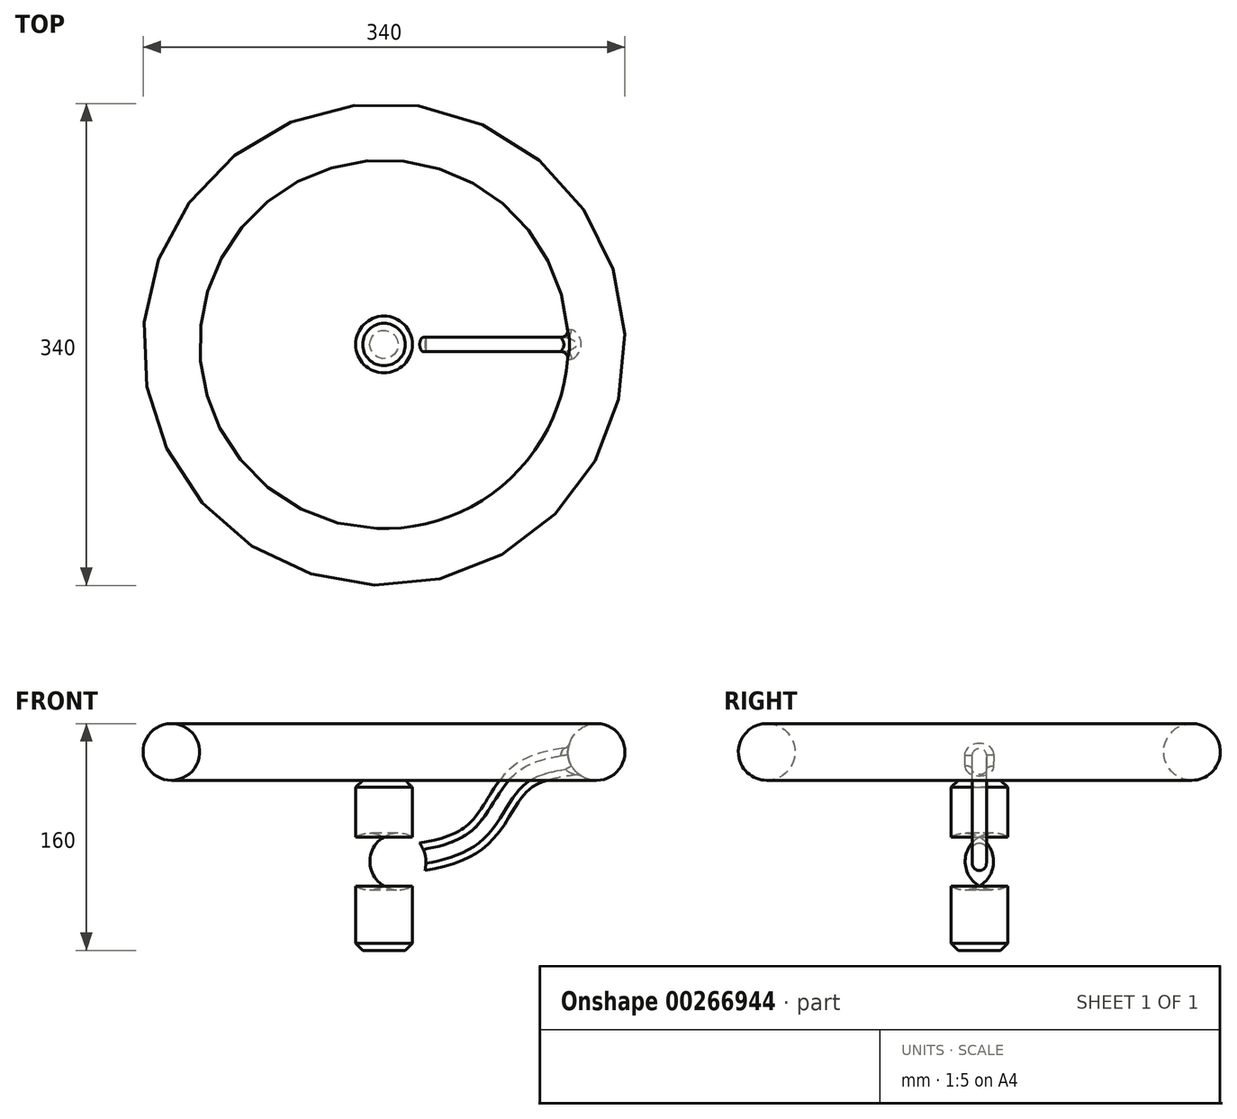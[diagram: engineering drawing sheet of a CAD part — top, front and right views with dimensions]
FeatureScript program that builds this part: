
annotation { "Feature Type Name" : "Feature", "Feature Type Description" : "" }
export const myFeature = defineFeature(function(context is Context, id is Id, definition is map)
    precondition{}
    {
        {
            var Q0;
            Q0=qCreatedBy(makeId("Front.planeOp"),FACE);
            var sketch = newSketch(context, id + "F0", { "sketchPlane" : qUnion([Q0])});
            skLineSegment(sketch, "E0", {"start": v(0, 60) * mm, "end": v(0, -60) * mm});
            skLineSegment(sketch, "E1", {"start": v(0, -60) * mm, "end": v(20, -60) * mm});
            skLineSegment(sketch, "E2", {"start": v(20, -60) * mm, "end": v(20, -14.64) * mm});
            skLineSegment(sketch, "E3", {"start": v(0, 60) * mm, "end": v(20, 60) * mm});
            skLineSegment(sketch, "E4", {"start": v(20, 60) * mm, "end": v(20, 20) * mm});
            skArc(sketch, "E5", {"start": v(20, -14.64) * mm, "mid": v(30, 2.68) * mm, "end": v(20, 20) * mm});
            skSolve(sketch);
        }
        {
            var Q0;
            Q0 = qSketchRegion(id + "F0", true);
            var Q1;
            Q1=sQuery(id+"F0.wireOp",EDGE,"E0");
            revolve(context, id + "F1", {"entities" : qUnion([Q0]), "axis" : qUnion([Q1]), "revolveType" : RevolveType.FULL});
        }
        {
            var Q0;
            Q0=makeQuery(id+"F1.opRevolve","SWEPT_EDGE",EDGE,{"disambiguationData":[OSD([sQuery(id+"F0.wireOp",EDGE,"E3"),sQuery(id+"F0.wireOp",EDGE,"E4")])]});
            var Q1;
            Q1=makeQuery(id+"F1.opRevolve","SWEPT_EDGE",EDGE,{"disambiguationData":[OSD([sQuery(id+"F0.wireOp",EDGE,"E1"),sQuery(id+"F0.wireOp",EDGE,"E2")])]});
            chamfer(context, id + "F2", {"entities" : qUnion([Q0, Q1]), "width" : 5 * mm, "tangentPropagation" : true});
        }
        {
            var Q0;
            Q0=qCreatedBy(makeId("Right.planeOp"),FACE);
            cPlane(context, id + "F3", {"entities" : qUnion([Q0]), "cplaneType" : CPlaneType.OFFSET, "offset" : 20 * mm, "width" : 150 * mm, "height" : 150 * mm});
        }
        {
            var Q0;
            Q0=qCreatedBy(id+"F3.planeOp",FACE);
            var sketch = newSketch(context, id + "F4", { "sketchPlane" : qUnion([Q0])});
            skLineSegment(sketch, "E6.bottom", {"start": v(0, -5) * mm, "end": v(0, -5) * mm});
            skLineSegment(sketch, "E6.top", {"start": v(0, 15) * mm, "end": v(0, 15) * mm});
            skLineSegment(sketch, "E6.left", {"start": v(5, 0) * mm, "end": v(5, 10) * mm});
            skLineSegment(sketch, "E6.right", {"start": v(-5, 0) * mm, "end": v(-5, 10) * mm});
            skPoint(sketch, "E6.middle", {"position": v(0, 5) * mm});
            skPoint(sketch, "E7.visualSharp", {"position": v(5, 15) * mm});
            skArc(sketch, "E7.filletArc", {"start": v(5, 10) * mm, "mid": v(3.54, 13.54) * mm, "end": v(0, 15) * mm});
            skPoint(sketch, "E8.visualSharp", {"position": v(-5, 15) * mm});
            skArc(sketch, "E8.filletArc", {"start": v(0, 15) * mm, "mid": v(-3.54, 13.54) * mm, "end": v(-5, 10) * mm});
            skPoint(sketch, "E9.visualSharp", {"position": v(-5, -5) * mm});
            skArc(sketch, "E9.filletArc", {"start": v(-5, 0) * mm, "mid": v(-3.54, -3.54) * mm, "end": v(0, -5) * mm});
            skPoint(sketch, "E10.visualSharp", {"position": v(5, -5) * mm});
            skArc(sketch, "E10.filletArc", {"start": v(0, -5) * mm, "mid": v(3.54, -3.54) * mm, "end": v(5, 0) * mm});
            skSolve(sketch);
        }
        {
            var Q0;
            Q0=qCreatedBy(makeId("Front.planeOp"),FACE);
            var sketch = newSketch(context, id + "F5", { "sketchPlane" : qUnion([Q0])});
            skFitSpline(sketch, "E11", {"points": [v(20.08, 5.28) * mm, v(66.4, 22.18) * mm, v(96.37, 61.72) * mm, v(150, 76.2) * mm], "startDerivative": vector(146.82, 19.14) * mm, "endDerivative": vector(191.33, 30.59) * mm});
            skSolve(sketch);
        }
        {
            var Q0;
            Q0 = qSketchRegion(id + "F4", true);
            var Q1;
            Q1 = qConstructionFilter(qBodyType(qCreatedBy(id + "F5" ,EDGE), BodyType.WIRE), ConstructionObject.NO);
            sweep(context, id + "F6", {"operationType" : NewBodyOperationType.ADD, "profiles" : qUnion([Q0]), "path" : qUnion([Q1])});
        }
        {
            var Q0;
            Q0=qCreatedBy(makeId("Front.planeOp"),FACE);
            var sketch = newSketch(context, id + "F7", { "sketchPlane" : qUnion([Q0])});
            skCircle(sketch, "E12", {"center": v(150, 80) * mm, "radius": 20 * mm});
            skSolve(sketch);
        }
        {
            var Q0;
            Q0 = qSketchRegion(id + "F7", true);
            var Q1;
            Q1=makeQuery(id+"F1.opRevolve","SWEPT_FACE",FACE,{"disambiguationData":[OSD([sQuery(id+"F0.wireOp",EDGE,"E4")])]});
            revolve(context, id + "F8", {"operationType" : NewBodyOperationType.ADD, "entities" : qUnion([Q0]), "axis" : qUnion([Q1]), "revolveType" : RevolveType.FULL});
        }
        {
            var Q0;
            Q0=makeQuery(id+"F8.boolean.opBoolean","INTERSECT",EDGE,{"derivedFrom":[makeQuery(id+"FtabRh7vFhWOj5B_1.1.F6.opSweep","SWEPT_FACE",FACE,{"disambiguationData":[OSD([sQuery(id+"F4.wireOp",EDGE,"E7.filletArc"),sQuery(id+"F4.wireOp",EDGE,"E8.filletArc"),sQuery(id+"F5.wireOp",EDGE,"E11")])]}),makeQuery(id+"F8.opRevolve","SWEPT_FACE",FACE,{"disambiguationData":[OSD([sQuery(id+"F7.wireOp",EDGE,"E12")])]})]});
            var Q1;
            Q1=makeQuery(id+"F8.boolean.opBoolean","INTERSECT",EDGE,{"derivedFrom":[makeQuery(id+"F6.opSweep","SWEPT_FACE",FACE,{"disambiguationData":[OSD([sQuery(id+"F4.wireOp",EDGE,"E7.filletArc"),sQuery(id+"F4.wireOp",EDGE,"E8.filletArc"),sQuery(id+"F5.wireOp",EDGE,"E11")])]}),makeQuery(id+"F8.opRevolve","SWEPT_FACE",FACE,{"disambiguationData":[OSD([sQuery(id+"F7.wireOp",EDGE,"E12")])]})]});
            var Q2;
            Q2=makeQuery(id+"F8.boolean.opBoolean","INTERSECT",EDGE,{"derivedFrom":[makeQuery(id+"FtabRh7vFhWOj5B_1.4.F6.opSweep","SWEPT_FACE",FACE,{"disambiguationData":[OSD([sQuery(id+"F4.wireOp",EDGE,"E7.filletArc"),sQuery(id+"F4.wireOp",EDGE,"E8.filletArc"),sQuery(id+"F5.wireOp",EDGE,"E11")])]}),makeQuery(id+"F8.opRevolve","SWEPT_FACE",FACE,{"disambiguationData":[OSD([sQuery(id+"F7.wireOp",EDGE,"E12")])]})]});
            var Q3;
            Q3=makeQuery(id+"F8.boolean.opBoolean","INTERSECT",EDGE,{"derivedFrom":[makeQuery(id+"FtabRh7vFhWOj5B_1.3.F6.opSweep","SWEPT_FACE",FACE,{"disambiguationData":[OSD([sQuery(id+"F4.wireOp",EDGE,"E7.filletArc"),sQuery(id+"F4.wireOp",EDGE,"E8.filletArc"),sQuery(id+"F5.wireOp",EDGE,"E11")])]}),makeQuery(id+"F8.opRevolve","SWEPT_FACE",FACE,{"disambiguationData":[OSD([sQuery(id+"F7.wireOp",EDGE,"E12")])]})]});
            var Q4;
            Q4=makeQuery(id+"F8.boolean.opBoolean","INTERSECT",EDGE,{"derivedFrom":[makeQuery(id+"FtabRh7vFhWOj5B_1.2.F6.opSweep","SWEPT_FACE",FACE,{"disambiguationData":[OSD([sQuery(id+"F4.wireOp",EDGE,"E7.filletArc"),sQuery(id+"F4.wireOp",EDGE,"E8.filletArc"),sQuery(id+"F5.wireOp",EDGE,"E11")])]}),makeQuery(id+"F8.opRevolve","SWEPT_FACE",FACE,{"disambiguationData":[OSD([sQuery(id+"F7.wireOp",EDGE,"E12")])]})]});
            fillet(context, id + "F9", {"entities" : qUnion([Q0, Q1, Q2, Q3, Q4]), "radius" : 5 * mm, "tangentPropagation" : true, "allowEdgeOverflow" : false});
        }
    });
